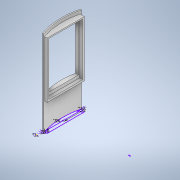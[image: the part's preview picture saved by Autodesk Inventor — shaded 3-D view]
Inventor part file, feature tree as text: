
AUTODESK INVENTOR PART (.ipt)
format: ipt  version: 2022 (Build 260153000, 153)  size: 163,840 bytes
history: native  units: mm
features: extrude x8, sketch x1
ambient origin geometry x8: Origin, YZ Plane, XZ Plane, XY Plane, X Axis, Y Axis, Z Axis, Center Point
bodies: Body1 (feature_tree)
feature tree (9):
  sketch  "Sketch1"  dims[d1=2.0mm d3=2.0mm d4=2.0mm d5=2.0mm d6=32.0mm d8=3.6mm d9=2.0mm d10=2.5mm d11=2.0mm d12=5.0mm d29=1.7mm d37=138.0mm d38=0.0mm d39=133.0mm d40=0.0mm d41=129.0mm d42=0.0mm d43=131.0mm d44=0.0mm d45=129.0mm d46=0.0mm d47=51.0mm d48=0.0mm d49=46.0mm d50=0.0mm d53=43.0mm d54=0.0mm]
  extrude  "Extrusion12"  Depth=43.0mm
  extrude  "Extrusion13"  Depth=2.0mm
  extrude  "Extrusion14"  Depth=43.0mm
  extrude  "Extrusion15"  Depth=2.0mm
  extrude  "Extrusion16"  Depth=5.0mm
  extrude  "Extrusion17"  Depth=1.7mm
  extrude  "Extrusion18"  Depth=138.0mm TaperAngle=0.0deg
  extrude  "Extrusion20"  Depth=133.0mm TaperAngle=0.0deg
